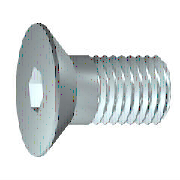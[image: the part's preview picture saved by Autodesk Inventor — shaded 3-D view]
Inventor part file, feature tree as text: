
AUTODESK INVENTOR PART (.ipt)
format: ipt  version: 2020 (Build 240168000, 168)  size: 185,344 bytes
history: native  units: mm (DEFAULTED — no unit token found)
features: other x4, sketch x3, fillet x1, chamfer x1
ambient origin geometry x8: Origin, YZ Plane, XZ Plane, XY Plane, X Axis, Y Axis, Z Axis, Center Point
bodies: Solid1 (feature_tree)
feature tree (9):
  sketch  "Sketch1"  dims[d2=3.0mm]
  other  "WorkPoint1"
  sketch  "Sketch2"  dims[d3=3.0mm]
  fillet  "Fillet1"  [1 undecoded]
  chamfer  "Chamfer1"  Distance=1.5mm
  other  "MSC_A1"
  other  "MSC_PF1"
  other  "MSC_PT1"
  sketch  "Sketch3"  dims[d4=1.5mm d5=1.5mm d6=8.0mm d7=30.0mm d8=360.0deg d9=0.0mm d10=2.0mm d11=2.0mm d12=120.0deg d13=120.0deg d14=120.0deg d15=120.0deg d16=1.2mm d17=0.0mm d18=0.1mm d19=0.25mm d20=45.0deg d22=0.0mm d23=0.0mm d35=0.0mm d37=0.0mm d38=0.0mm d39=0.25mm d40=0.0mm d41=0.0mm d42=0.0mm d43=45.0deg]
note: 1 required parameter value undecoded (feature->parameter linkage not recoverable at this tier; creation-order binding heuristic only, values carry confidence <= 0.55)
